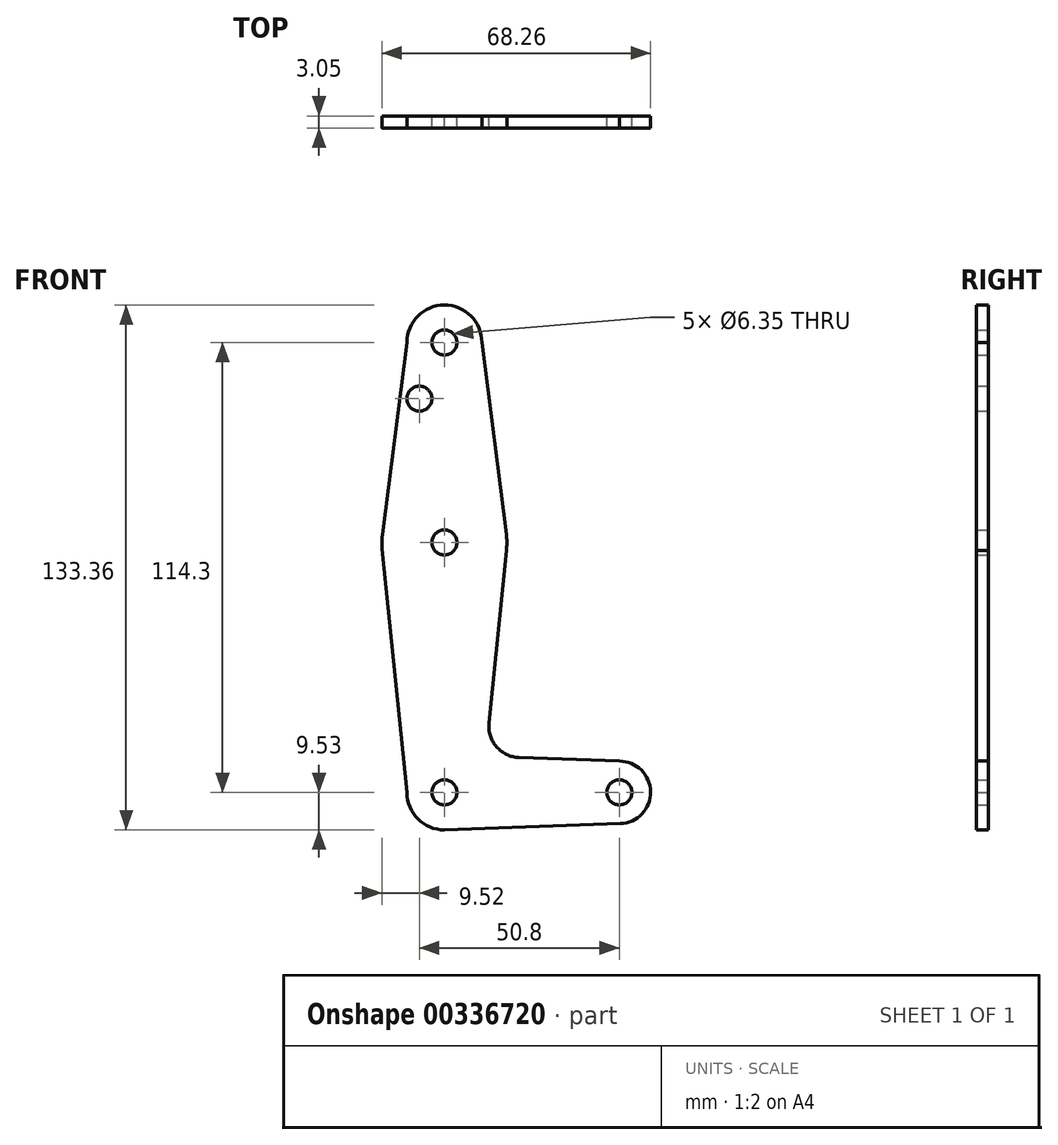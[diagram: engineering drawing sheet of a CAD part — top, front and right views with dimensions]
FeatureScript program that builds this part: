
annotation { "Feature Type Name" : "Feature", "Feature Type Description" : "" }
export const myFeature = defineFeature(function(context is Context, id is Id, definition is map)
    precondition{}
    {
        {
            var Q0;
            Q0=qCreatedBy(makeId("Front.planeOp"),FACE);
            var sketch = newSketch(context, id + "F0", { "sketchPlane" : qUnion([Q0])});
            skLineSegment(sketch, "E0", {"start": v(0, 0) * mm, "end": v(0, 114.3) * mm});
            skLineSegment(sketch, "E1", {"start": v(0, 0) * mm, "end": v(44.45, 0) * mm});
            skCircle(sketch, "E2", {"center": v(44.45, 0) * mm, "radius": 7.94 * mm});
            skCircle(sketch, "E3", {"center": v(0, 0) * mm, "radius": 9.53 * mm});
            skCircle(sketch, "E4", {"center": v(0, 63.5) * mm, "radius": 15.88 * mm});
            skCircle(sketch, "E5", {"center": v(0, 114.3) * mm, "radius": 9.53 * mm});
            skLineSegment(sketch, "E6", {"start": v(9.52, 114.3) * mm, "end": v(15.75, 65.5) * mm});
            skLineSegment(sketch, "E7", {"start": v(-9.53, 114.3) * mm, "end": v(-15.75, 65.5) * mm});
            skLineSegment(sketch, "E8", {"start": v(-9.52, 0) * mm, "end": v(-15.8, 61.9) * mm});
            skCircle(sketch, "E9", {"center": v(0, 114.3) * mm, "radius": 3.18 * mm});
            skCircle(sketch, "E10", {"center": v(0, 63.5) * mm, "radius": 3.18 * mm});
            skCircle(sketch, "E11", {"center": v(0, 0) * mm, "radius": 3.18 * mm});
            skCircle(sketch, "E12", {"center": v(44.45, 0) * mm, "radius": 3.18 * mm});
            skCircle(sketch, "E13", {"center": v(-6.35, 100.03) * mm, "radius": 3.18 * mm});
            skLineSegment(sketch, "E14", {"start": v(44.45, 7.94) * mm, "end": v(18.96, 8.85) * mm});
            skLineSegment(sketch, "E15", {"start": v(0, -9.53) * mm, "end": v(44.73, -7.93) * mm});
            skPoint(sketch, "E16.newPointB", {"position": v(0, 9.53) * mm});
            skLineSegment(sketch, "E17", {"start": v(15.75, 61.5) * mm, "end": v(11.34, 17.6) * mm});
            skArc(sketch, "E18.filletArc", {"start": v(11.34, 17.6) * mm, "mid": v(13.26, 11.57) * mm, "end": v(18.96, 8.85) * mm});
            skSolve(sketch);
        }
        {
            var Q0;
            {var subQ5=sQuery(id+"F0.wireOp",EDGE,"E6");Q0=makeQuery(id+"F0.imprint","IMPRINT",FACE,{"disambiguationData":[TD([[makeQuery(id+"F0.imprint","IMPRINT",EDGE,{"derivedFrom":subQ5}),-1.0]])]});}
            var Q1;
            {var subQ0=sQuery(id+"F0.wireOp",EDGE,"E7");Q1=makeQuery(id+"F0.imprint","IMPRINT",FACE,{"disambiguationData":[TD([[makeQuery(id+"F0.imprint","IMPRINT",EDGE,{"derivedFrom":subQ0}),1.0]])]});}
            var Q2;
            Q2=makeQuery(id+"F0.imprint","IMPRINT",FACE,{"disambiguationData":[TD([[makeQuery(id+"F0.imprint","IMPRINT",EDGE,{"derivedFrom":sQuery(id+"F0.wireOp",EDGE,"E9")}),-1.0]])]});
            var Q3;
            {var subQ7=sQuery(id+"F0.wireOp",EDGE,"E14");Q3=makeQuery(id+"F0.imprint","IMPRINT",FACE,{"disambiguationData":[TD([[makeQuery(id+"F0.imprint","IMPRINT",EDGE,{"derivedFrom":subQ7}),1.0]])]});}
            var Q4;
            {var subQ0=sQuery(id+"F0.wireOp",EDGE,"E4");var subQ2=sQuery(id+"F0.wireOp",EDGE,"E0");var subQ3=makeQuery(id+"F0.imprint","INTERSECT",VERTEX,{"disambiguationData":[OD(0.0)],"derivedFrom":[subQ2,subQ0]});Q4=makeQuery(id+"F0.imprint","IMPRINT",FACE,{"disambiguationData":[TD([[makeQuery(id+"F0.imprint","IMPRINT",EDGE,{"disambiguationData":[TD([[subQ3,-1.0]])],"derivedFrom":subQ2}),-1.0]])]});}
            var Q5;
            {var subQ0=sQuery(id+"F0.wireOp",EDGE,"E4");var subQ2=sQuery(id+"F0.wireOp",EDGE,"E0");var subQ8=makeQuery(id+"F0.imprint","INTERSECT",VERTEX,{"disambiguationData":[OD(0.0)],"derivedFrom":[subQ2,subQ0]});Q5=makeQuery(id+"F0.imprint","IMPRINT",FACE,{"disambiguationData":[TD([[makeQuery(id+"F0.imprint","IMPRINT",EDGE,{"disambiguationData":[TD([[subQ8,-1.0]])],"derivedFrom":subQ2}),1.0]])]});}
            var Q6;
            {var subQ5=sQuery(id+"F0.wireOp",EDGE,"E8");Q6=makeQuery(id+"F0.imprint","IMPRINT",FACE,{"disambiguationData":[TD([[makeQuery(id+"F0.imprint","IMPRINT",EDGE,{"derivedFrom":subQ5}),-1.0]])]});}
            var Q7;
            {var subQ4=sQuery(id+"F0.wireOp",EDGE,"E0");var subQ6=sQuery(id+"F0.wireOp",EDGE,"E11");var subQ10=makeQuery(id+"F0.imprint","INTERSECT",VERTEX,{"derivedFrom":[subQ4,subQ6]});Q7=makeQuery(id+"F0.imprint","IMPRINT",FACE,{"disambiguationData":[TD([[makeQuery(id+"F0.imprint","IMPRINT",EDGE,{"disambiguationData":[TD([[subQ10,-1.0]])],"derivedFrom":subQ4}),1.0]])]});}
            var Q8;
            {var subQ0=sQuery(id+"F0.wireOp",EDGE,"E2");var subQ1=sQuery(id+"F0.wireOp",EDGE,"E1");var subQ2=makeQuery(id+"F0.imprint","INTERSECT",VERTEX,{"derivedFrom":[subQ1,subQ0]});Q8=makeQuery(id+"F0.imprint","IMPRINT",FACE,{"disambiguationData":[TD([[makeQuery(id+"F0.imprint","IMPRINT",EDGE,{"disambiguationData":[TD([[subQ2,1.0]])],"derivedFrom":subQ1}),-1.0]])]});}
            var Q9;
            Q9=makeQuery(id+"F0.imprint","IMPRINT",FACE,{"disambiguationData":[TD([[makeQuery(id+"F0.imprint","IMPRINT",EDGE,{"derivedFrom":sQuery(id+"F0.wireOp",EDGE,"E12")}),-1.0]])]});
            var Q10;
            {var subQ0=sQuery(id+"F0.wireOp",EDGE,"E11");var subQ1=sQuery(id+"F0.wireOp",EDGE,"E0");var subQ2=makeQuery(id+"F0.imprint","INTERSECT",VERTEX,{"derivedFrom":[subQ1,subQ0]});Q10=makeQuery(id+"F0.imprint","IMPRINT",FACE,{"disambiguationData":[TD([[makeQuery(id+"F0.imprint","IMPRINT",EDGE,{"disambiguationData":[TD([[subQ2,-1.0]])],"derivedFrom":subQ1}),-1.0]])]});}
            extrude(context, id + "F1", {"entities" : qUnion([Q0, Q1, Q2, Q3, Q4, Q5, Q6, Q7, Q8, Q9, Q10]), "depth" : 3.05 * mm});
        }
    });
